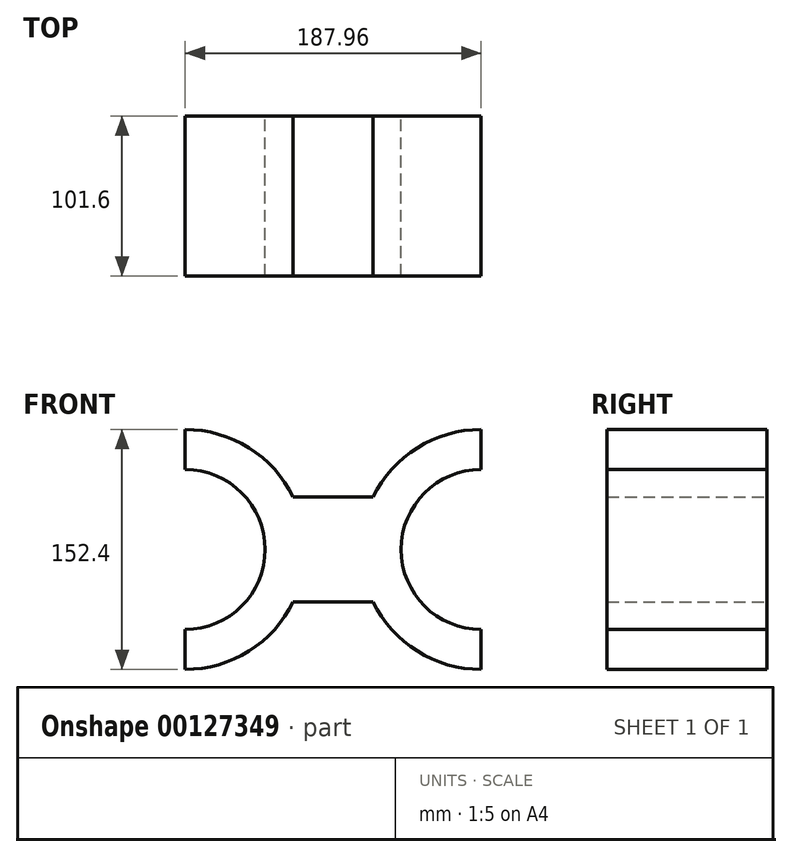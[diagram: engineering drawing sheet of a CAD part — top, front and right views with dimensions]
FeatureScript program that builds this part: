
annotation { "Feature Type Name" : "Feature", "Feature Type Description" : "" }
export const myFeature = defineFeature(function(context is Context, id is Id, definition is map)
    precondition{}
    {
        {
            var Q0;
            Q0=qCreatedBy(makeId("Front.planeOp"),FACE);
            var sketch = newSketch(context, id + "F0", { "sketchPlane" : qUnion([Q0])});
            skLineSegment(sketch, "E0.left", {"start": v(93.98, -76.2) * mm, "end": v(93.98, -50.8) * mm});
            skLineSegment(sketch, "E0.right", {"start": v(-93.98, -76.2) * mm, "end": v(-93.98, -50.8) * mm});
            skPoint(sketch, "E0.middle", {"position": v(0, 0) * mm});
            skArc(sketch, "E1", {"start": v(93.98, 76.2) * mm, "mid": v(53.51, 64.57) * mm, "end": v(25.4, 33.21) * mm});
            skArc(sketch, "E2", {"start": v(-93.98, -76.2) * mm, "mid": v(-53.51, -64.57) * mm, "end": v(-25.4, -33.21) * mm});
            skArc(sketch, "E3", {"start": v(-93.98, -50.8) * mm, "mid": v(-43.18, 0) * mm, "end": v(-93.98, 50.8) * mm});
            skArc(sketch, "E4", {"start": v(93.98, 50.8) * mm, "mid": v(43.18, 0) * mm, "end": v(93.98, -50.8) * mm});
            skLineSegment(sketch, "E5.trimOffspring", {"start": v(-93.98, 50.8) * mm, "end": v(-93.98, 76.2) * mm});
            skLineSegment(sketch, "E6.trimOffspring", {"start": v(93.98, 50.8) * mm, "end": v(93.98, 76.2) * mm});
            skLineSegment(sketch, "E7.bottom", {"start": v(-25.4, 33.21) * mm, "end": v(25.4, 33.21) * mm});
            skLineSegment(sketch, "E7.top", {"start": v(-25.4, -33.21) * mm, "end": v(25.4, -33.21) * mm});
            skLineSegment(sketch, "E7.left", {"start": v(-25.4, -33.21) * mm, "end": v(-25.4, -33.21) * mm});
            skArc(sketch, "E8.trimOffspring", {"start": v(25.4, -33.21) * mm, "mid": v(53.51, -64.57) * mm, "end": v(93.98, -76.2) * mm});
            skArc(sketch, "E9.trimOffspring", {"start": v(-25.4, 33.21) * mm, "mid": v(-53.51, 64.57) * mm, "end": v(-93.98, 76.2) * mm});
            skSolve(sketch);
        }
        {
            var Q0;
            Q0 = qSketchRegion(id + "F0", true);
            extrude(context, id + "F1", {"entities" : qUnion([Q0]), "depth" : 101.6 * mm});
        }
    });
